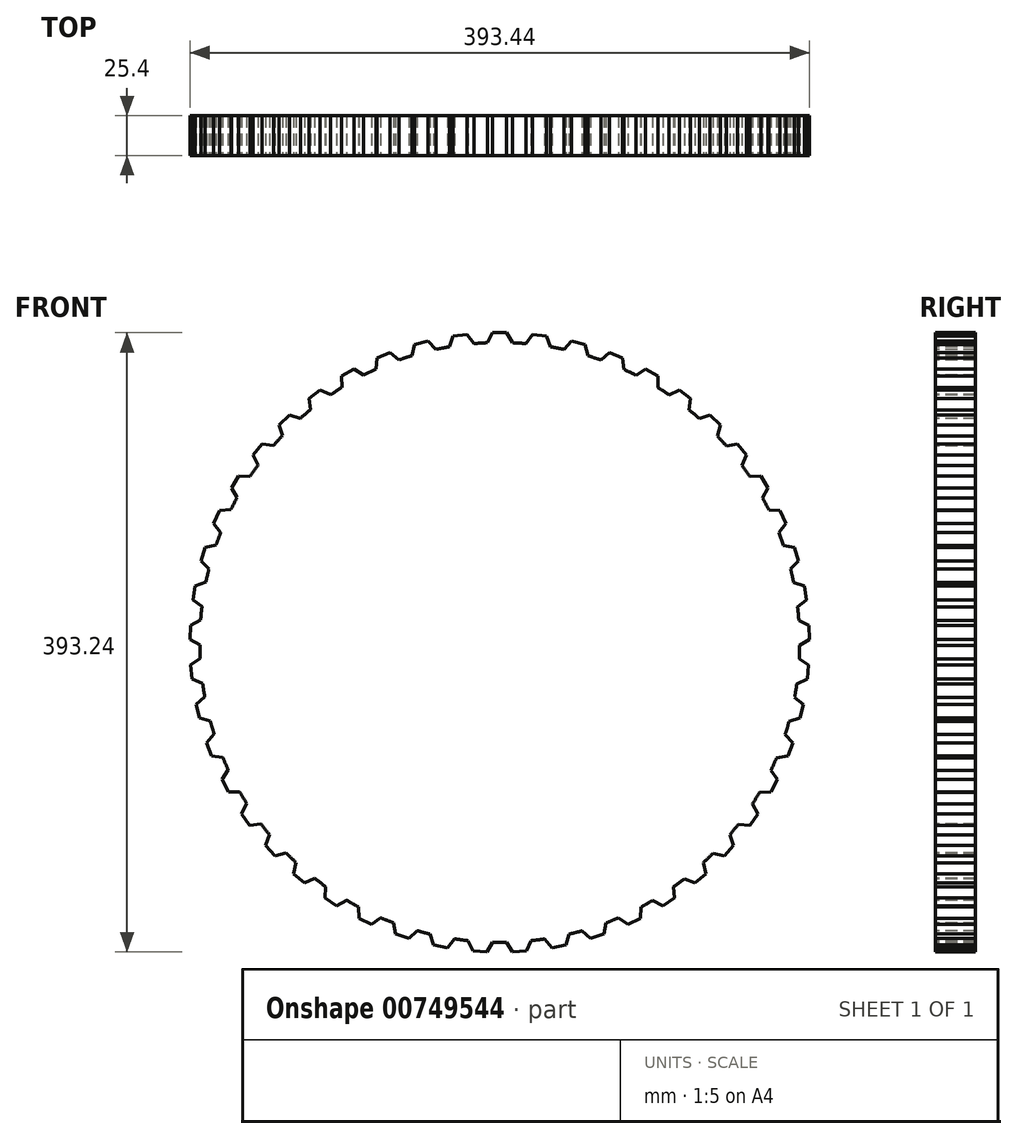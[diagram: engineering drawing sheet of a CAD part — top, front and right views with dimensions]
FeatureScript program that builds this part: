
annotation { "Feature Type Name" : "Feature", "Feature Type Description" : "" }
export const myFeature = defineFeature(function(context is Context, id is Id, definition is map)
    precondition{}
    {
        {
            var Q0;
            Q0=qCreatedBy(makeId("Front.planeOp"),FACE);
            var sketch = newSketch(context, id + "F0", { "sketchPlane" : qUnion([Q0])});
            skArc(sketch, "E0", {"start": v(-32.02, 187.79) * mm, "mid": v(-36.3, 187.01) * mm, "end": v(-40.54, 186.14) * mm});
            skLineSegment(sketch, "E1", {"start": v(-4.45, 196.68) * mm, "end": v(4.44, 196.68) * mm});
            skLineSegment(sketch, "E2", {"start": v(-4.45, 196.68) * mm, "end": v(-7.75, 190.34) * mm});
            skLineSegment(sketch, "E3", {"start": v(4.44, 196.68) * mm, "end": v(8, 190.33) * mm});
            skPoint(sketch, "E4.orphan", {"position": v(0, 196.68) * mm});
            skLineSegment(sketch, "E5.1.0", {"start": v(-20.74, 195.64) * mm, "end": v(-16.4, 189.8) * mm});
            skLineSegment(sketch, "E5.1.1", {"start": v(-29.56, 194.5) * mm, "end": v(-20.74, 195.64) * mm});
            skLineSegment(sketch, "E5.1.2", {"start": v(-29.56, 194.5) * mm, "end": v(-32.02, 187.79) * mm});
            skLineSegment(sketch, "E5.2.0", {"start": v(-45.59, 191.38) * mm, "end": v(-40.54, 186.14) * mm});
            skLineSegment(sketch, "E5.2.1", {"start": v(-54.19, 189.12) * mm, "end": v(-45.59, 191.38) * mm});
            skLineSegment(sketch, "E5.2.2", {"start": v(-54.19, 189.12) * mm, "end": v(-55.77, 182.15) * mm});
            skLineSegment(sketch, "E5.3.0", {"start": v(-69.69, 183.98) * mm, "end": v(-64, 179.42) * mm});
            skLineSegment(sketch, "E5.3.1", {"start": v(-77.93, 180.64) * mm, "end": v(-69.69, 183.98) * mm});
            skLineSegment(sketch, "E5.3.2", {"start": v(-77.93, 180.64) * mm, "end": v(-78.61, 173.52) * mm});
            skLineSegment(sketch, "E5.4.0", {"start": v(-92.64, 173.55) * mm, "end": v(-86.43, 169.77) * mm});
            skLineSegment(sketch, "E5.4.1", {"start": v(-100.39, 169.2) * mm, "end": v(-92.64, 173.55) * mm});
            skLineSegment(sketch, "E5.4.2", {"start": v(-100.39, 169.2) * mm, "end": v(-100.15, 162.05) * mm});
            skLineSegment(sketch, "E5.5.0", {"start": v(-114.08, 160.28) * mm, "end": v(-107.43, 157.32) * mm});
            skLineSegment(sketch, "E5.5.1", {"start": v(-121.2, 154.96) * mm, "end": v(-114.08, 160.28) * mm});
            skLineSegment(sketch, "E5.5.2", {"start": v(-121.2, 154.96) * mm, "end": v(-120.05, 147.9) * mm});
            skLineSegment(sketch, "E5.6.0", {"start": v(-133.64, 144.38) * mm, "end": v(-126.66, 142.3) * mm});
            skLineSegment(sketch, "E5.6.1", {"start": v(-140.02, 138.2) * mm, "end": v(-133.64, 144.38) * mm});
            skLineSegment(sketch, "E5.6.2", {"start": v(-140.02, 138.2) * mm, "end": v(-137.98, 131.34) * mm});
            skLineSegment(sketch, "E5.7.0", {"start": v(-151, 126.1) * mm, "end": v(-143.82, 124.93) * mm});
            skLineSegment(sketch, "E5.7.1", {"start": v(-156.54, 119.15) * mm, "end": v(-151, 126.1) * mm});
            skLineSegment(sketch, "E5.7.2", {"start": v(-156.54, 119.15) * mm, "end": v(-153.65, 112.62) * mm});
            skLineSegment(sketch, "E5.8.0", {"start": v(-165.89, 105.76) * mm, "end": v(-158.61, 105.5) * mm});
            skLineSegment(sketch, "E5.8.1", {"start": v(-170.5, 98.16) * mm, "end": v(-165.89, 105.76) * mm});
            skLineSegment(sketch, "E5.8.2", {"start": v(-170.5, 98.16) * mm, "end": v(-166.79, 92.05) * mm});
            skLineSegment(sketch, "E5.9.0", {"start": v(-178.05, 83.68) * mm, "end": v(-170.8, 84.36) * mm});
            skLineSegment(sketch, "E5.9.1", {"start": v(-181.65, 75.55) * mm, "end": v(-178.05, 83.68) * mm});
            skLineSegment(sketch, "E5.9.2", {"start": v(-181.65, 75.55) * mm, "end": v(-177.19, 69.96) * mm});
            skLineSegment(sketch, "E5.10.0", {"start": v(-187.29, 60.22) * mm, "end": v(-180.19, 61.82) * mm});
            skLineSegment(sketch, "E5.10.1", {"start": v(-189.82, 51.7) * mm, "end": v(-187.29, 60.22) * mm});
            skLineSegment(sketch, "E5.10.2", {"start": v(-189.82, 51.7) * mm, "end": v(-184.68, 46.73) * mm});
            skLineSegment(sketch, "E5.11.0", {"start": v(-193.45, 35.78) * mm, "end": v(-186.62, 38.28) * mm});
            skLineSegment(sketch, "E5.11.1", {"start": v(-194.87, 27) * mm, "end": v(-193.45, 35.78) * mm});
            skLineSegment(sketch, "E5.11.2", {"start": v(-194.87, 27) * mm, "end": v(-189.14, 22.73) * mm});
            skLineSegment(sketch, "E5.12.0", {"start": v(-196.44, 10.75) * mm, "end": v(-189.98, 14.1) * mm});
            skLineSegment(sketch, "E5.12.1", {"start": v(-196.72, 1.86) * mm, "end": v(-196.44, 10.75) * mm});
            skLineSegment(sketch, "E5.12.2", {"start": v(-196.72, 1.86) * mm, "end": v(-190.5, -1.64) * mm});
            skLineSegment(sketch, "E5.13.0", {"start": v(-196.2, -14.46) * mm, "end": v(-190.22, -10.31) * mm});
            skLineSegment(sketch, "E5.13.1", {"start": v(-195.35, -23.31) * mm, "end": v(-196.2, -14.46) * mm});
            skLineSegment(sketch, "E5.13.2", {"start": v(-195.35, -23.31) * mm, "end": v(-188.72, -25.99) * mm});
            skLineSegment(sketch, "E5.14.0", {"start": v(-192.74, -39.43) * mm, "end": v(-187.34, -34.55) * mm});
            skLineSegment(sketch, "E5.14.1", {"start": v(-190.76, -48.1) * mm, "end": v(-192.74, -39.43) * mm});
            skLineSegment(sketch, "E5.14.2", {"start": v(-190.76, -48.1) * mm, "end": v(-183.85, -49.9) * mm});
            skLineSegment(sketch, "E5.15.0", {"start": v(-186.11, -63.76) * mm, "end": v(-181.38, -58.23) * mm});
            skLineSegment(sketch, "E5.15.1", {"start": v(-183.04, -72.1) * mm, "end": v(-186.11, -63.76) * mm});
            skLineSegment(sketch, "E5.15.2", {"start": v(-183.04, -72.1) * mm, "end": v(-175.95, -73) * mm});
            skLineSegment(sketch, "E5.16.0", {"start": v(-176.43, -87.03) * mm, "end": v(-172.45, -80.94) * mm});
            skLineSegment(sketch, "E5.16.1", {"start": v(-172.32, -94.91) * mm, "end": v(-176.43, -87.03) * mm});
            skLineSegment(sketch, "E5.16.2", {"start": v(-172.32, -94.91) * mm, "end": v(-165.17, -94.9) * mm});
            skLineSegment(sketch, "E5.17.0", {"start": v(-163.86, -108.88) * mm, "end": v(-160.68, -102.33) * mm});
            skLineSegment(sketch, "E5.17.1", {"start": v(-158.77, -116.17) * mm, "end": v(-163.86, -108.88) * mm});
            skLineSegment(sketch, "E5.17.2", {"start": v(-158.77, -116.17) * mm, "end": v(-151.68, -115.25) * mm});
            skLineSegment(sketch, "E5.18.0", {"start": v(-148.59, -128.94) * mm, "end": v(-146.28, -122.04) * mm});
            skLineSegment(sketch, "E5.18.1", {"start": v(-142.61, -135.52) * mm, "end": v(-148.59, -128.94) * mm});
            skLineSegment(sketch, "E5.18.2", {"start": v(-142.61, -135.52) * mm, "end": v(-135.7, -133.7) * mm});
            skLineSegment(sketch, "E5.19.0", {"start": v(-130.88, -146.88) * mm, "end": v(-129.47, -139.74) * mm});
            skLineSegment(sketch, "E5.19.1", {"start": v(-124.11, -152.64) * mm, "end": v(-130.88, -146.88) * mm});
            skLineSegment(sketch, "E5.19.2", {"start": v(-124.11, -152.64) * mm, "end": v(-117.49, -149.96) * mm});
            skLineSegment(sketch, "E5.20.0", {"start": v(-111.02, -162.41) * mm, "end": v(-110.54, -155.15) * mm});
            skLineSegment(sketch, "E5.20.1", {"start": v(-103.57, -167.26) * mm, "end": v(-111.02, -162.41) * mm});
            skLineSegment(sketch, "E5.20.2", {"start": v(-103.57, -167.26) * mm, "end": v(-97.35, -163.75) * mm});
            skLineSegment(sketch, "E5.21.0", {"start": v(-89.34, -175.28) * mm, "end": v(-89.8, -168.01) * mm});
            skLineSegment(sketch, "E5.21.1", {"start": v(-81.33, -179.13) * mm, "end": v(-89.34, -175.28) * mm});
            skLineSegment(sketch, "E5.21.2", {"start": v(-81.33, -179.13) * mm, "end": v(-75.6, -174.85) * mm});
            skLineSegment(sketch, "E5.22.0", {"start": v(-66.2, -185.26) * mm, "end": v(-67.57, -178.11) * mm});
            skLineSegment(sketch, "E5.22.1", {"start": v(-57.76, -188.06) * mm, "end": v(-66.2, -185.26) * mm});
            skLineSegment(sketch, "E5.22.2", {"start": v(-57.76, -188.06) * mm, "end": v(-52.63, -183.09) * mm});
            skLineSegment(sketch, "E5.23.0", {"start": v(-41.96, -192.2) * mm, "end": v(-44.24, -185.3) * mm});
            skLineSegment(sketch, "E5.23.1", {"start": v(-33.23, -193.9) * mm, "end": v(-41.96, -192.2) * mm});
            skLineSegment(sketch, "E5.23.2", {"start": v(-33.23, -193.9) * mm, "end": v(-28.78, -188.31) * mm});
            skLineSegment(sketch, "E5.24.0", {"start": v(-17.04, -196) * mm, "end": v(-20.18, -189.43) * mm});
            skLineSegment(sketch, "E5.24.1", {"start": v(-8.17, -196.56) * mm, "end": v(-17.04, -196) * mm});
            skLineSegment(sketch, "E5.24.2", {"start": v(-8.17, -196.56) * mm, "end": v(-4.46, -190.45) * mm});
            skLineSegment(sketch, "E5.25.0", {"start": v(8.17, -196.56) * mm, "end": v(4.21, -190.45) * mm});
            skLineSegment(sketch, "E5.25.1", {"start": v(17.04, -196) * mm, "end": v(8.17, -196.56) * mm});
            skLineSegment(sketch, "E5.25.2", {"start": v(17.04, -196) * mm, "end": v(19.93, -189.45) * mm});
            skLineSegment(sketch, "E5.26.0", {"start": v(33.23, -193.9) * mm, "end": v(28.53, -188.35) * mm});
            skLineSegment(sketch, "E5.26.1", {"start": v(41.96, -192.2) * mm, "end": v(33.23, -193.9) * mm});
            skLineSegment(sketch, "E5.26.2", {"start": v(41.96, -192.2) * mm, "end": v(43.99, -185.35) * mm});
            skLineSegment(sketch, "E5.27.0", {"start": v(57.76, -188.06) * mm, "end": v(52.38, -183.16) * mm});
            skLineSegment(sketch, "E5.27.1", {"start": v(66.2, -185.26) * mm, "end": v(57.76, -188.06) * mm});
            skLineSegment(sketch, "E5.27.2", {"start": v(66.2, -185.26) * mm, "end": v(67.33, -178.2) * mm});
            skLineSegment(sketch, "E5.28.0", {"start": v(81.33, -179.13) * mm, "end": v(75.37, -174.95) * mm});
            skLineSegment(sketch, "E5.28.1", {"start": v(89.34, -175.28) * mm, "end": v(81.33, -179.13) * mm});
            skLineSegment(sketch, "E5.28.2", {"start": v(89.34, -175.28) * mm, "end": v(89.57, -168.13) * mm});
            skLineSegment(sketch, "E5.29.0", {"start": v(103.57, -167.26) * mm, "end": v(97.13, -163.88) * mm});
            skLineSegment(sketch, "E5.29.1", {"start": v(111.02, -162.41) * mm, "end": v(103.57, -167.26) * mm});
            skLineSegment(sketch, "E5.29.2", {"start": v(111.02, -162.41) * mm, "end": v(110.33, -155.3) * mm});
            skLineSegment(sketch, "E5.30.0", {"start": v(124.11, -152.64) * mm, "end": v(117.29, -150.11) * mm});
            skLineSegment(sketch, "E5.30.1", {"start": v(130.88, -146.88) * mm, "end": v(124.11, -152.64) * mm});
            skLineSegment(sketch, "E5.30.2", {"start": v(130.88, -146.88) * mm, "end": v(129.28, -139.91) * mm});
            skLineSegment(sketch, "E5.31.0", {"start": v(142.61, -135.52) * mm, "end": v(135.52, -133.88) * mm});
            skLineSegment(sketch, "E5.31.1", {"start": v(148.59, -128.94) * mm, "end": v(142.61, -135.52) * mm});
            skLineSegment(sketch, "E5.31.2", {"start": v(148.59, -128.94) * mm, "end": v(146.11, -122.23) * mm});
            skLineSegment(sketch, "E5.32.0", {"start": v(158.77, -116.17) * mm, "end": v(151.53, -115.45) * mm});
            skLineSegment(sketch, "E5.32.1", {"start": v(163.86, -108.88) * mm, "end": v(158.77, -116.17) * mm});
            skLineSegment(sketch, "E5.32.2", {"start": v(163.86, -108.88) * mm, "end": v(160.55, -102.54) * mm});
            skLineSegment(sketch, "E5.33.0", {"start": v(172.32, -94.91) * mm, "end": v(165.05, -95.13) * mm});
            skLineSegment(sketch, "E5.33.1", {"start": v(176.43, -87.03) * mm, "end": v(172.32, -94.91) * mm});
            skLineSegment(sketch, "E5.33.2", {"start": v(176.43, -87.03) * mm, "end": v(172.34, -81.17) * mm});
            skLineSegment(sketch, "E5.34.0", {"start": v(183.04, -72.1) * mm, "end": v(175.86, -73.24) * mm});
            skLineSegment(sketch, "E5.34.1", {"start": v(186.11, -63.76) * mm, "end": v(183.04, -72.1) * mm});
            skLineSegment(sketch, "E5.34.2", {"start": v(186.11, -63.76) * mm, "end": v(181.3, -58.47) * mm});
            skLineSegment(sketch, "E5.35.0", {"start": v(190.76, -48.1) * mm, "end": v(183.78, -50.15) * mm});
            skLineSegment(sketch, "E5.35.1", {"start": v(192.74, -39.43) * mm, "end": v(190.76, -48.1) * mm});
            skLineSegment(sketch, "E5.35.2", {"start": v(192.74, -39.43) * mm, "end": v(187.3, -34.8) * mm});
            skLineSegment(sketch, "E5.36.0", {"start": v(195.35, -23.31) * mm, "end": v(188.68, -26.24) * mm});
            skLineSegment(sketch, "E5.36.1", {"start": v(196.2, -14.46) * mm, "end": v(195.35, -23.31) * mm});
            skLineSegment(sketch, "E5.36.2", {"start": v(196.2, -14.46) * mm, "end": v(190.2, -10.57) * mm});
            skLineSegment(sketch, "E5.37.0", {"start": v(196.72, 1.86) * mm, "end": v(190.5, -1.9) * mm});
            skLineSegment(sketch, "E5.37.1", {"start": v(196.44, 10.75) * mm, "end": v(196.72, 1.86) * mm});
            skLineSegment(sketch, "E5.37.2", {"start": v(196.44, 10.75) * mm, "end": v(190, 13.84) * mm});
            skLineSegment(sketch, "E5.38.0", {"start": v(194.87, 27) * mm, "end": v(189.17, 22.48) * mm});
            skLineSegment(sketch, "E5.38.1", {"start": v(193.45, 35.78) * mm, "end": v(194.87, 27) * mm});
            skLineSegment(sketch, "E5.38.2", {"start": v(193.45, 35.78) * mm, "end": v(186.67, 38.03) * mm});
            skLineSegment(sketch, "E5.39.0", {"start": v(189.82, 51.7) * mm, "end": v(184.74, 46.48) * mm});
            skLineSegment(sketch, "E5.39.1", {"start": v(187.29, 60.22) * mm, "end": v(189.82, 51.7) * mm});
            skLineSegment(sketch, "E5.39.2", {"start": v(187.29, 60.22) * mm, "end": v(180.27, 61.58) * mm});
            skLineSegment(sketch, "E5.40.0", {"start": v(181.65, 75.55) * mm, "end": v(177.28, 69.73) * mm});
            skLineSegment(sketch, "E5.40.1", {"start": v(178.05, 83.68) * mm, "end": v(181.65, 75.55) * mm});
            skLineSegment(sketch, "E5.40.2", {"start": v(178.05, 83.68) * mm, "end": v(170.92, 84.13) * mm});
            skLineSegment(sketch, "E5.41.0", {"start": v(170.5, 98.16) * mm, "end": v(166.9, 91.82) * mm});
            skLineSegment(sketch, "E5.41.1", {"start": v(165.89, 105.76) * mm, "end": v(170.5, 98.16) * mm});
            skLineSegment(sketch, "E5.41.2", {"start": v(165.89, 105.76) * mm, "end": v(158.75, 105.3) * mm});
            skLineSegment(sketch, "E5.42.0", {"start": v(156.54, 119.15) * mm, "end": v(153.8, 112.41) * mm});
            skLineSegment(sketch, "E5.42.1", {"start": v(151, 126.1) * mm, "end": v(156.54, 119.15) * mm});
            skLineSegment(sketch, "E5.42.2", {"start": v(151, 126.1) * mm, "end": v(143.99, 124.73) * mm});
            skLineSegment(sketch, "E5.43.0", {"start": v(140.02, 138.2) * mm, "end": v(138.16, 131.16) * mm});
            skLineSegment(sketch, "E5.43.1", {"start": v(133.64, 144.38) * mm, "end": v(140.02, 138.2) * mm});
            skLineSegment(sketch, "E5.43.2", {"start": v(133.64, 144.38) * mm, "end": v(126.85, 142.12) * mm});
            skLineSegment(sketch, "E5.44.0", {"start": v(121.2, 154.96) * mm, "end": v(120.25, 147.75) * mm});
            skLineSegment(sketch, "E5.44.1", {"start": v(114.08, 160.28) * mm, "end": v(121.2, 154.96) * mm});
            skLineSegment(sketch, "E5.44.2", {"start": v(114.08, 160.28) * mm, "end": v(107.64, 157.18) * mm});
            skLineSegment(sketch, "E5.45.0", {"start": v(100.39, 169.2) * mm, "end": v(100.37, 161.91) * mm});
            skLineSegment(sketch, "E5.45.1", {"start": v(92.64, 173.55) * mm, "end": v(100.39, 169.2) * mm});
            skLineSegment(sketch, "E5.45.2", {"start": v(92.64, 173.55) * mm, "end": v(86.65, 169.65) * mm});
            skLineSegment(sketch, "E5.46.0", {"start": v(77.93, 180.64) * mm, "end": v(78.84, 173.42) * mm});
            skLineSegment(sketch, "E5.46.1", {"start": v(69.69, 183.98) * mm, "end": v(77.93, 180.64) * mm});
            skLineSegment(sketch, "E5.46.2", {"start": v(69.69, 183.98) * mm, "end": v(64.25, 179.34) * mm});
            skLineSegment(sketch, "E5.47.0", {"start": v(54.19, 189.12) * mm, "end": v(56.02, 182.08) * mm});
            skLineSegment(sketch, "E5.47.1", {"start": v(45.59, 191.38) * mm, "end": v(54.19, 189.12) * mm});
            skLineSegment(sketch, "E5.47.2", {"start": v(45.59, 191.38) * mm, "end": v(40.79, 186.08) * mm});
            skLineSegment(sketch, "E5.48.0", {"start": v(29.56, 194.5) * mm, "end": v(32.27, 187.75) * mm});
            skLineSegment(sketch, "E5.48.1", {"start": v(20.74, 195.64) * mm, "end": v(29.56, 194.5) * mm});
            skLineSegment(sketch, "E5.48.2", {"start": v(20.74, 195.64) * mm, "end": v(16.66, 189.77) * mm});
            skArc(sketch, "E6.trimOffspring", {"start": v(-7.75, 190.34) * mm, "mid": v(-12.08, 190.12) * mm, "end": v(-16.4, 189.8) * mm});
            skArc(sketch, "E7.trimOffspring", {"start": v(-55.77, 182.15) * mm, "mid": v(-59.9, 180.84) * mm, "end": v(-64, 179.42) * mm});
            skArc(sketch, "E8.trimOffspring", {"start": v(-100.15, 162.05) * mm, "mid": v(-103.82, 159.73) * mm, "end": v(-107.43, 157.32) * mm});
            skArc(sketch, "E9.trimOffspring", {"start": v(16.66, 189.77) * mm, "mid": v(12.33, 190.1) * mm, "end": v(8, 190.33) * mm});
            skArc(sketch, "E10.trimOffspring", {"start": v(40.79, 186.08) * mm, "mid": v(36.54, 186.96) * mm, "end": v(32.27, 187.75) * mm});
            skArc(sketch, "E11.trimOffspring", {"start": v(64.25, 179.34) * mm, "mid": v(60.15, 180.76) * mm, "end": v(56.02, 182.08) * mm});
            skArc(sketch, "E12.trimOffspring", {"start": v(86.65, 169.65) * mm, "mid": v(82.77, 171.58) * mm, "end": v(78.84, 173.42) * mm});
            skArc(sketch, "E13.trimOffspring", {"start": v(107.64, 157.18) * mm, "mid": v(104.03, 159.59) * mm, "end": v(100.37, 161.91) * mm});
            skArc(sketch, "E14.trimOffspring", {"start": v(-120.05, 147.9) * mm, "mid": v(-123.4, 145.14) * mm, "end": v(-126.66, 142.3) * mm});
            skArc(sketch, "E15.trimOffspring", {"start": v(-137.98, 131.34) * mm, "mid": v(-140.94, 128.17) * mm, "end": v(-143.82, 124.93) * mm});
            skArc(sketch, "E16.trimOffspring", {"start": v(-153.65, 112.62) * mm, "mid": v(-156.17, 109.1) * mm, "end": v(-158.61, 105.5) * mm});
            skArc(sketch, "E17.trimOffspring", {"start": v(-166.79, 92.05) * mm, "mid": v(-168.84, 88.23) * mm, "end": v(-170.8, 84.36) * mm});
            skArc(sketch, "E18.trimOffspring", {"start": v(-177.19, 69.96) * mm, "mid": v(-178.73, 65.91) * mm, "end": v(-180.19, 61.82) * mm});
            skArc(sketch, "E19.trimOffspring", {"start": v(-184.68, 46.73) * mm, "mid": v(-185.7, 42.51) * mm, "end": v(-186.62, 38.28) * mm});
            skArc(sketch, "E20.trimOffspring", {"start": v(-189.14, 22.73) * mm, "mid": v(-189.6, 18.42) * mm, "end": v(-189.98, 14.1) * mm});
            skArc(sketch, "E21.trimOffspring", {"start": v(-190.5, -1.64) * mm, "mid": v(-190.4, -5.98) * mm, "end": v(-190.22, -10.31) * mm});
            skArc(sketch, "E22.trimOffspring", {"start": v(-188.72, -25.99) * mm, "mid": v(-188.08, -30.28) * mm, "end": v(-187.34, -34.55) * mm});
            skArc(sketch, "E23.trimOffspring", {"start": v(-183.85, -49.9) * mm, "mid": v(-182.66, -54.08) * mm, "end": v(-181.38, -58.23) * mm});
            skArc(sketch, "E24.trimOffspring", {"start": v(-175.95, -73) * mm, "mid": v(-174.25, -77) * mm, "end": v(-172.45, -80.94) * mm});
            skArc(sketch, "E25.trimOffspring", {"start": v(-165.17, -94.9) * mm, "mid": v(-162.97, -98.65) * mm, "end": v(-160.68, -102.33) * mm});
            skArc(sketch, "E26.trimOffspring", {"start": v(-151.68, -115.25) * mm, "mid": v(-149.02, -118.68) * mm, "end": v(-146.28, -122.04) * mm});
            skArc(sketch, "E27.trimOffspring", {"start": v(-135.7, -133.7) * mm, "mid": v(-132.62, -136.76) * mm, "end": v(-129.47, -139.74) * mm});
            skArc(sketch, "E28.trimOffspring", {"start": v(-117.49, -149.96) * mm, "mid": v(-114.04, -152.6) * mm, "end": v(-110.54, -155.15) * mm});
            skArc(sketch, "E29.trimOffspring", {"start": v(-97.35, -163.75) * mm, "mid": v(-93.6, -165.92) * mm, "end": v(-89.8, -168.01) * mm});
            skArc(sketch, "E30.trimOffspring", {"start": v(-75.6, -174.85) * mm, "mid": v(-71.6, -176.53) * mm, "end": v(-67.57, -178.11) * mm});
            skArc(sketch, "E31.trimOffspring", {"start": v(-52.63, -183.09) * mm, "mid": v(-48.44, -184.24) * mm, "end": v(-44.24, -185.3) * mm});
            skArc(sketch, "E32.trimOffspring", {"start": v(-28.78, -188.31) * mm, "mid": v(-24.49, -188.92) * mm, "end": v(-20.18, -189.43) * mm});
            skArc(sketch, "E33.trimOffspring", {"start": v(-4.46, -190.45) * mm, "mid": v(-0.13, -190.5) * mm, "end": v(4.21, -190.45) * mm});
            skArc(sketch, "E34.trimOffspring", {"start": v(19.93, -189.45) * mm, "mid": v(24.23, -188.95) * mm, "end": v(28.53, -188.35) * mm});
            skArc(sketch, "E35.trimOffspring", {"start": v(43.99, -185.35) * mm, "mid": v(48.2, -184.3) * mm, "end": v(52.38, -183.16) * mm});
            skArc(sketch, "E36.trimOffspring", {"start": v(67.33, -178.2) * mm, "mid": v(71.37, -176.63) * mm, "end": v(75.37, -174.95) * mm});
            skArc(sketch, "E37.trimOffspring", {"start": v(89.57, -168.13) * mm, "mid": v(93.37, -166.05) * mm, "end": v(97.13, -163.88) * mm});
            skArc(sketch, "E38.trimOffspring", {"start": v(110.33, -155.3) * mm, "mid": v(113.84, -152.75) * mm, "end": v(117.29, -150.11) * mm});
            skArc(sketch, "E39.trimOffspring", {"start": v(129.28, -139.91) * mm, "mid": v(132.44, -136.93) * mm, "end": v(135.52, -133.88) * mm});
            skArc(sketch, "E40.trimOffspring", {"start": v(146.11, -122.23) * mm, "mid": v(148.86, -118.87) * mm, "end": v(151.53, -115.45) * mm});
            skArc(sketch, "E41.trimOffspring", {"start": v(160.55, -102.54) * mm, "mid": v(162.84, -98.86) * mm, "end": v(165.05, -95.13) * mm});
            skArc(sketch, "E42.trimOffspring", {"start": v(181.3, -58.47) * mm, "mid": v(182.6, -54.32) * mm, "end": v(183.78, -50.15) * mm});
            skArc(sketch, "E43.trimOffspring", {"start": v(172.34, -81.17) * mm, "mid": v(174.14, -77.23) * mm, "end": v(175.86, -73.24) * mm});
            skArc(sketch, "E44.trimOffspring", {"start": v(190.2, -10.57) * mm, "mid": v(190.4, -6.23) * mm, "end": v(190.5, -1.9) * mm});
            skArc(sketch, "E45.trimOffspring", {"start": v(187.3, -34.8) * mm, "mid": v(188.04, -30.53) * mm, "end": v(188.68, -26.24) * mm});
            skArc(sketch, "E46.trimOffspring", {"start": v(190, 13.84) * mm, "mid": v(189.63, 18.17) * mm, "end": v(189.17, 22.48) * mm});
            skArc(sketch, "E47.trimOffspring", {"start": v(186.67, 38.03) * mm, "mid": v(185.75, 42.27) * mm, "end": v(184.74, 46.48) * mm});
            skArc(sketch, "E48.trimOffspring", {"start": v(170.92, 84.13) * mm, "mid": v(168.96, 88) * mm, "end": v(166.9, 91.82) * mm});
            skArc(sketch, "E49.trimOffspring", {"start": v(126.85, 142.12) * mm, "mid": v(123.58, 144.97) * mm, "end": v(120.25, 147.75) * mm});
            skArc(sketch, "E50.trimOffspring", {"start": v(143.99, 124.73) * mm, "mid": v(141.1, 127.98) * mm, "end": v(138.16, 131.16) * mm});
            skArc(sketch, "E51.trimOffspring", {"start": v(158.75, 105.3) * mm, "mid": v(156.32, 108.88) * mm, "end": v(153.8, 112.41) * mm});
            skLineSegment(sketch, "E52", {"start": v(180.27, 61.58) * mm, "end": v(177.28, 69.73) * mm});
            skLineSegment(sketch, "E53", {"start": v(-86.43, 169.77) * mm, "end": v(-78.61, 173.52) * mm});
            skSolve(sketch);
        }
        {
            var Q0;
            Q0=makeQuery(id+"F0.imprint","IMPRINT",FACE,{"disambiguationData":[TD([[makeQuery(id+"F0.imprint","IMPRINT",EDGE,{"derivedFrom":sQuery(id+"F0.wireOp",EDGE,"E0")}),1.0]])]});
            extrude(context, id + "F1", {"entities" : qUnion([Q0]), "endBound" : BoundingType.SYMMETRIC, "oppositeDirection" : true, "depth" : 25.4 * mm, "offsetDistance" : 25.4 * mm});
        }
        {
            var Q0;
            Q0=qCreatedBy(makeId("Front.planeOp"),FACE);
            var sketch = newSketch(context, id + "F2", { "sketchPlane" : qUnion([Q0])});
            skCircle(sketch, "E54", {"center": v(0, 0) * mm, "radius": 19.05 * mm});
            skSolve(sketch);
        }
        {
            var Q0;
            Q0=sQuery(id+"F2.wireOp",EDGE,"E54");
            extrude(context, id + "F3", {"bodyType" : ToolBodyType.SURFACE, "surfaceEntities" : qUnion([Q0]), "endBound" : BoundingType.SYMMETRIC, "depth" : 25.4 * mm, "offsetDistance" : 25.4 * mm});
        }
    });
